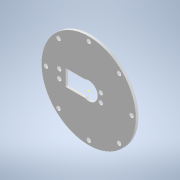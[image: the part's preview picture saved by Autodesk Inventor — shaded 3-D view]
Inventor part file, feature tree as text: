
AUTODESK INVENTOR PART (.ipt)
format: ipt  version: 2021 (Build 250183000, 183)  size: 136,704 bytes
history: native  units: mm
features: sketch x3, extrude x2, other x1
ambient origin geometry x8: Origin, YZ Plane, XZ Plane, XY Plane, X Axis, Y Axis, Z Axis, Center Point
bodies: Body1 (feature_tree)
feature tree (6):
  other  "Sólido1"
  extrude  "Extrusión1"  Depth=3.0mm TaperAngle=0.0deg
  sketch  "Boceto2"  dims[d24=3.0mm d25=0.0mm]
  extrude  "Extrusión2"  [1 undecoded]
  sketch  "Boceto1"  dims[d5=80.0mm d7=360.0deg d18=3.0mm d19=0.0mm]
  sketch  "Boceto3"
note: 1 required parameter value undecoded (feature->parameter linkage not recoverable at this tier; creation-order binding heuristic only, values carry confidence <= 0.55)
